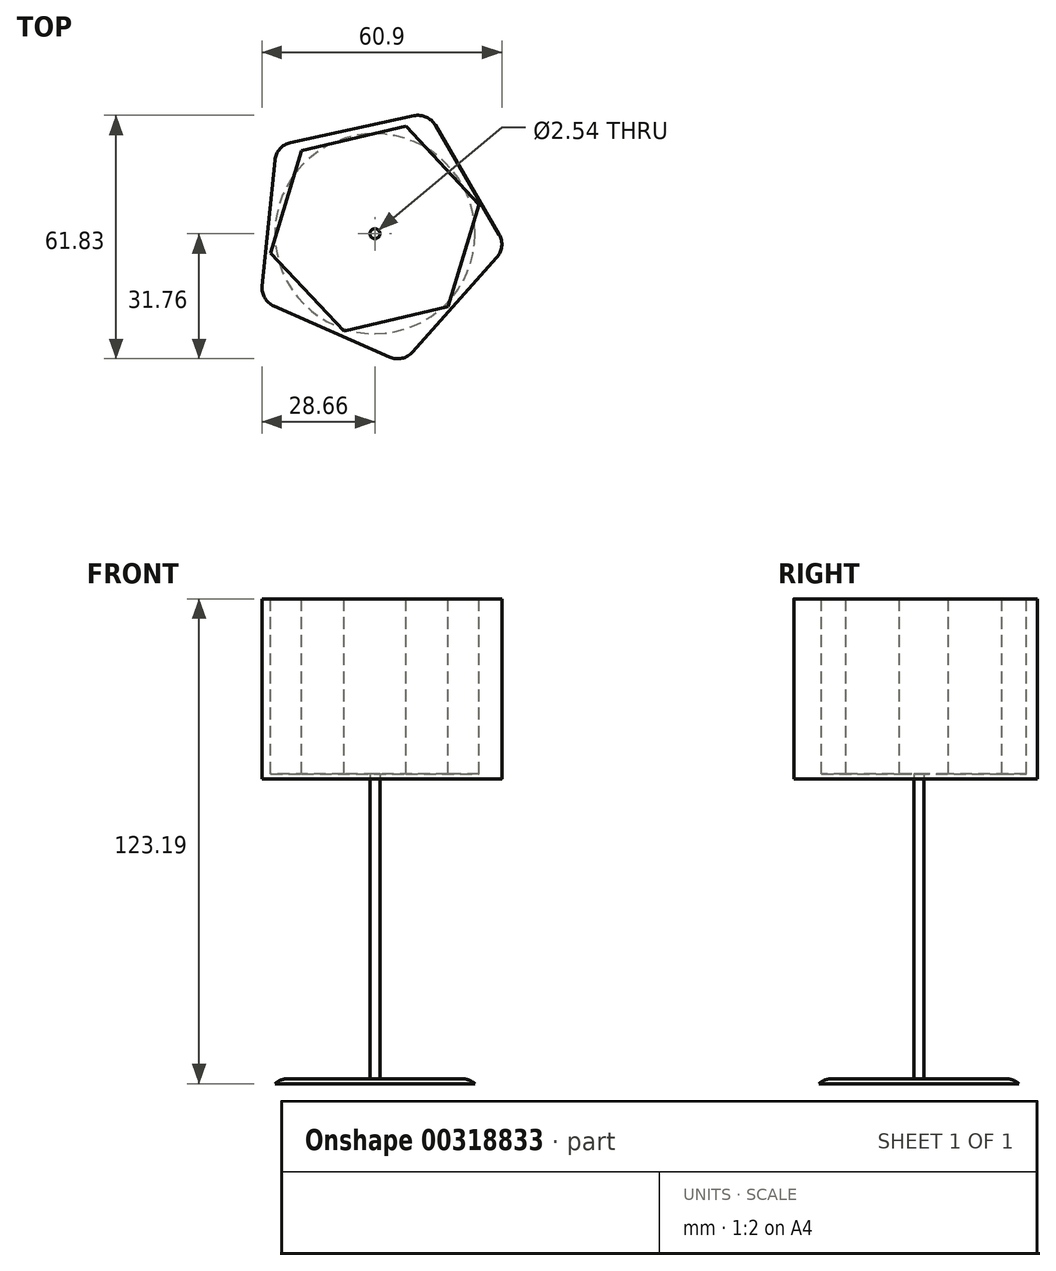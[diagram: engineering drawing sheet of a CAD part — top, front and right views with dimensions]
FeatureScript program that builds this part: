
annotation { "Feature Type Name" : "Feature", "Feature Type Description" : "" }
export const myFeature = defineFeature(function(context is Context, id is Id, definition is map)
    precondition{}
    {
        {
            var Q0;
            Q0=qCreatedBy(makeId("Top.planeOp"),FACE);
            var sketch = newSketch(context, id + "F0", { "sketchPlane" : qUnion([Q0])});
            skCircle(sketch, "E0", {"center": v(0, 0) * mm, "radius": 25.4 * mm});
            skSolve(sketch);
        }
        {
            var Q0;
            Q0 = qSketchRegion(id + "F0", true);
            extrude(context, id + "F1", {"entities" : qUnion([Q0]), "depth" : 1.27 * mm});
        }
        {
            var Q0;
            Q0=makeQuery(id+"F1.opExtrude","CAP_EDGE",EDGE,{"disambiguationData":[OSD([sQuery(id+"F0.wireOp",EDGE,"E0")])],"isStart":false});
            fillet(context, id + "F2", {"entities" : qUnion([Q0]), "radius" : 5.08 * mm, "tangentPropagation" : true, "allowEdgeOverflow" : false});
        }
        {
            var Q0;
            Q0=makeQuery(id+"F1.opExtrude","CAP_FACE",FACE,{"disambiguationData":[OSD([sQuery(id+"F0.wireOp",EDGE,"E0")])],"isStart":false});
            var sketch = newSketch(context, id + "F3", { "sketchPlane" : qUnion([Q0])});
            skCircle(sketch, "E1", {"center": v(0, 0) * mm, "radius": 1.27 * mm});
            skSolve(sketch);
        }
        {
            var Q0;
            Q0 = qSketchRegion(id + "F3", true);
            extrude(context, id + "F4", {"entities" : qUnion([Q0]), "operationType" : NewBodyOperationType.ADD, "depth" : 76.2 * mm});
        }
        {
            var Q0;
            Q0=makeQuery(id+"F4.opExtrude","CAP_FACE",FACE,{"disambiguationData":[OSD([sQuery(id+"F3.wireOp",EDGE,"E1")])],"isStart":false});
            var sketch = newSketch(context, id + "F5", { "sketchPlane" : qUnion([Q0])});
            skCircle(sketch, "E2.cCircle", {"center": v(0, 0) * mm, "radius": 27.16 * mm, "construction": true});
            skLineSegment(sketch, "E2.0", {"start": v(33.4, -3.36) * mm, "end": v(7.13, -32.81) * mm});
            skLineSegment(sketch, "E2.1", {"start": v(7.13, -32.81) * mm, "end": v(-29, -16.92) * mm});
            skLineSegment(sketch, "E2.2", {"start": v(-29, -16.92) * mm, "end": v(-25.05, 22.35) * mm});
            skLineSegment(sketch, "E2.3", {"start": v(-25.05, 22.35) * mm, "end": v(13.52, 30.73) * mm});
            skLineSegment(sketch, "E2.4", {"start": v(13.52, 30.73) * mm, "end": v(33.4, -3.36) * mm});
            skPoint(sketch, "E2.0.midPoint", {"position": v(20.27, -18.09) * mm});
            skSolve(sketch);
        }
        {
            var Q0;
            Q0=makeQuery(id+"F5.imprint","IMPRINT",FACE,{"disambiguationData":[TD([[makeQuery(id+"F5.imprint","IMPRINT",EDGE,{"derivedFrom":sQuery(id+"F5.wireOp",EDGE,"E2.0")}),-1.0]])]});
            extrude(context, id + "F6", {"entities" : qUnion([Q0]), "depth" : 45.72 * mm});
        }
        {
            var Q0;
            Q0=makeQuery(id+"F6.opExtrude","CAP_FACE",FACE,{"disambiguationData":[OSD([sQuery(id+"F3.wireOp",EDGE,"E1"),sQuery(id+"F5.wireOp",EDGE,"E2.0"),sQuery(id+"F5.wireOp",EDGE,"E2.1"),sQuery(id+"F5.wireOp",EDGE,"E2.2"),sQuery(id+"F5.wireOp",EDGE,"E2.3"),sQuery(id+"F5.wireOp",EDGE,"E2.4")])],"isStart":false});
            var sketch = newSketch(context, id + "F7", { "sketchPlane" : qUnion([Q0])});
            skCircle(sketch, "E3.cCircle", {"center": v(0, 1.27) * mm, "radius": 23.55 * mm, "construction": true});
            skLineSegment(sketch, "E3.0", {"start": v(26.48, 7.45) * mm, "end": v(18.6, -18.57) * mm});
            skLineSegment(sketch, "E3.1", {"start": v(18.6, -18.57) * mm, "end": v(-7.89, -24.75) * mm});
            skLineSegment(sketch, "E3.2", {"start": v(-7.89, -24.75) * mm, "end": v(-26.48, -4.9) * mm});
            skLineSegment(sketch, "E3.3", {"start": v(-26.48, -4.9) * mm, "end": v(-18.6, 21.11) * mm});
            skLineSegment(sketch, "E3.4", {"start": v(-18.6, 21.11) * mm, "end": v(7.89, 27.3) * mm});
            skLineSegment(sketch, "E3.5", {"start": v(7.89, 27.3) * mm, "end": v(26.48, 7.45) * mm});
            skPoint(sketch, "E3.0.midPoint", {"position": v(22.54, -5.56) * mm});
            skSolve(sketch);
        }
        {
            var Q0;
            Q0 = qSketchRegion(id + "F7", true);
            extrude(context, id + "F8", {"entities" : qUnion([Q0]), "operationType" : NewBodyOperationType.REMOVE, "oppositeDirection" : true, "depth" : 44.45 * mm});
        }
        {
            var Q0;
            Q0=makeQuery(id+"F6.opExtrude","SWEPT_EDGE",EDGE,{"disambiguationData":[OSD([sQuery(id+"F5.wireOp",EDGE,"E2.0"),sQuery(id+"F5.wireOp",EDGE,"E2.4")])]});
            fillet(context, id + "F9", {"entities" : qUnion([Q0]), "radius" : 5.08 * mm, "tangentPropagation" : true, "allowEdgeOverflow" : false});
        }
        {
            var Q0;
            Q0=makeQuery(id+"F6.opExtrude","SWEPT_EDGE",EDGE,{"disambiguationData":[OSD([sQuery(id+"F5.wireOp",EDGE,"E2.0"),sQuery(id+"F5.wireOp",EDGE,"E2.1")])]});
            fillet(context, id + "F10", {"entities" : qUnion([Q0]), "radius" : 5.08 * mm, "tangentPropagation" : true, "allowEdgeOverflow" : false});
        }
        {
            var Q0;
            Q0=makeQuery(id+"F6.opExtrude","SWEPT_EDGE",EDGE,{"disambiguationData":[OSD([sQuery(id+"F5.wireOp",EDGE,"E2.1"),sQuery(id+"F5.wireOp",EDGE,"E2.2")])]});
            fillet(context, id + "F11", {"entities" : qUnion([Q0]), "radius" : 5.08 * mm, "tangentPropagation" : true, "allowEdgeOverflow" : false});
        }
        {
            var Q0;
            Q0=makeQuery(id+"F6.opExtrude","SWEPT_EDGE",EDGE,{"disambiguationData":[OSD([sQuery(id+"F5.wireOp",EDGE,"E2.2"),sQuery(id+"F5.wireOp",EDGE,"E2.3")])]});
            fillet(context, id + "F12", {"entities" : qUnion([Q0]), "radius" : 5.08 * mm, "tangentPropagation" : true, "allowEdgeOverflow" : false});
        }
        {
            var Q0;
            Q0=makeQuery(id+"F6.opExtrude","SWEPT_EDGE",EDGE,{"disambiguationData":[OSD([sQuery(id+"F5.wireOp",EDGE,"E2.3"),sQuery(id+"F5.wireOp",EDGE,"E2.4")])]});
            fillet(context, id + "F13", {"entities" : qUnion([Q0]), "radius" : 5.08 * mm, "tangentPropagation" : true, "allowEdgeOverflow" : false});
        }
    });
